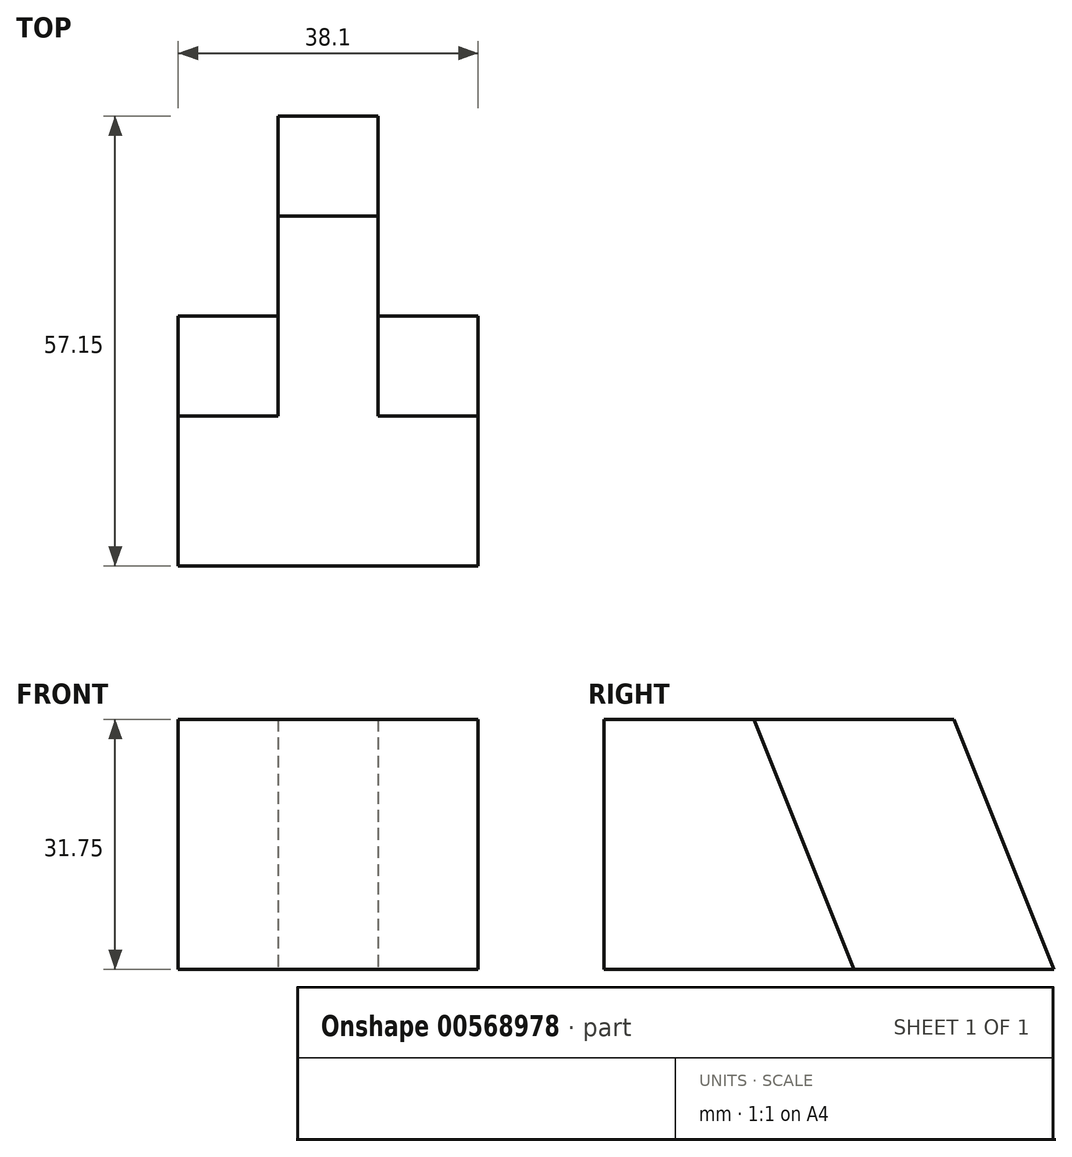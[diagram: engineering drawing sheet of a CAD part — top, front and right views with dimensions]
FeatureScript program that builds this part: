
annotation { "Feature Type Name" : "Feature", "Feature Type Description" : "" }
export const myFeature = defineFeature(function(context is Context, id is Id, definition is map)
    precondition{}
    {
        {
            var Q0;
            Q0=qCreatedBy(makeId("Top.planeOp"),FACE);
            var sketch = newSketch(context, id + "F0", { "sketchPlane" : qUnion([Q0])});
            skLineSegment(sketch, "E0", {"start": v(-16.45, -24.26) * mm, "end": v(21.65, -24.26) * mm});
            skLineSegment(sketch, "E1", {"start": v(21.65, -24.26) * mm, "end": v(21.65, 7.5) * mm});
            skLineSegment(sketch, "E2", {"start": v(21.65, 7.5) * mm, "end": v(8.95, 7.5) * mm});
            skLineSegment(sketch, "E3", {"start": v(8.95, 7.5) * mm, "end": v(8.95, 32.9) * mm});
            skLineSegment(sketch, "E4", {"start": v(8.95, 32.9) * mm, "end": v(-3.75, 32.9) * mm});
            skLineSegment(sketch, "E5", {"start": v(-3.75, 32.9) * mm, "end": v(-3.75, 7.5) * mm});
            skLineSegment(sketch, "E6", {"start": v(-3.75, 7.5) * mm, "end": v(-16.45, 7.5) * mm});
            skLineSegment(sketch, "E7", {"start": v(-16.45, 7.5) * mm, "end": v(-16.45, -24.26) * mm});
            skSolve(sketch);
        }
        {
            var Q0;
            Q0=makeQuery(id+"F0.imprint","IMPRINT",FACE,{"disambiguationData":[TD([[makeQuery(id+"F0.imprint","IMPRINT",EDGE,{"derivedFrom":sQuery(id+"F0.wireOp",EDGE,"E0")}),1.0]])]});
            var sketch = newSketch(context, id + "F1", { "sketchPlane" : qUnion([Q0])});
            skSolve(sketch);
        }
        {
            var Q0;
            Q0 = qSketchRegion(id + "F1", true);
            var Q1;
            Q1=makeQuery(id+"F0.imprint","IMPRINT",FACE,{"disambiguationData":[TD([[makeQuery(id+"F0.imprint","IMPRINT",EDGE,{"derivedFrom":sQuery(id+"F0.wireOp",EDGE,"E0")}),1.0]])]});
            extrude(context, id + "F2", {"entities" : qUnion([Q0, Q1]), "depth" : 31.75 * mm, "offsetDistance" : 25.4 * mm});
        }
        {
            var Q0;
            Q0=makeQuery(id+"F2.opExtrude","SWEPT_FACE",FACE,{"disambiguationData":[OSD([sQuery(id+"F0.wireOp",EDGE,"E5")])]});
            var sketch = newSketch(context, id + "F3", { "sketchPlane" : qUnion([Q0])});
            skLineSegment(sketch, "E8", {"start": v(-32.9, 31.75) * mm, "end": v(-20.2, 31.75) * mm});
            skLineSegment(sketch, "E9", {"start": v(-20.2, 31.75) * mm, "end": v(-32.9, 0) * mm});
            skLineSegment(sketch, "E10", {"start": v(-32.9, 0) * mm, "end": v(-32.9, 31.75) * mm});
            skLineSegment(sketch, "E11", {"start": v(-32.9, 31.75) * mm, "end": v(-32.9, 0) * mm});
            skSolve(sketch);
        }
        {
            var Q0;
            Q0 = qSketchRegion(id + "F3", true);
            extrude(context, id + "F4", {"entities" : qUnion([Q0]), "operationType" : NewBodyOperationType.REMOVE, "oppositeDirection" : true, "depth" : 12.7 * mm, "offsetDistance" : 25.4 * mm});
        }
        {
            var Q0;
            Q0=makeQuery(id+"F2.opExtrude","SWEPT_FACE",FACE,{"disambiguationData":[OSD([sQuery(id+"F0.wireOp",EDGE,"E7")])]});
            var sketch = newSketch(context, id + "F5", { "sketchPlane" : qUnion([Q0])});
            skLineSegment(sketch, "E12", {"start": v(-7.5, 0) * mm, "end": v(-7.5, 31.75) * mm});
            skLineSegment(sketch, "E13", {"start": v(-7.5, 31.75) * mm, "end": v(5.2, 31.75) * mm});
            skLineSegment(sketch, "E14", {"start": v(5.2, 31.75) * mm, "end": v(-7.5, 0) * mm});
            skSolve(sketch);
        }
        {
            var Q0;
            Q0 = qSketchRegion(id + "F5", true);
            extrude(context, id + "F6", {"entities" : qUnion([Q0]), "operationType" : NewBodyOperationType.REMOVE, "oppositeDirection" : true, "depth" : 12.7 * mm, "offsetDistance" : 25.4 * mm});
        }
        {
            var Q0;
            Q0=makeQuery(id+"F2.opExtrude","SWEPT_FACE",FACE,{"disambiguationData":[OSD([sQuery(id+"F0.wireOp",EDGE,"E1")])]});
            var sketch = newSketch(context, id + "F7", { "sketchPlane" : qUnion([Q0])});
            skLineSegment(sketch, "E15", {"start": v(7.5, 31.75) * mm, "end": v(-5.2, 31.75) * mm});
            skLineSegment(sketch, "E16", {"start": v(-5.2, 31.75) * mm, "end": v(7.5, 0) * mm});
            skLineSegment(sketch, "E17", {"start": v(7.5, 0) * mm, "end": v(7.5, 31.75) * mm});
            skSolve(sketch);
        }
        {
            var Q0;
            Q0 = qSketchRegion(id + "F7", true);
            extrude(context, id + "F8", {"entities" : qUnion([Q0]), "operationType" : NewBodyOperationType.REMOVE, "oppositeDirection" : true, "depth" : 12.7 * mm, "offsetDistance" : 25.4 * mm});
        }
    });
